# Revit family: TY-FRB-TY4131_Imperial
name_source: partatom
category: Sprinklers
revit_build: Autodesk Revit 2016 (Build: 20150220_1215(x64)
units: mm (PartAtom-declared; Revit-internal decimal feet)

## family parameters
Always vertical = Yes
Cut with Voids When Loaded = No
Maintain Annotation Orientation = No
OmniClass Number = 23.65.70.17.11.24
OmniClass Title = Fire Fighting Sprinkler Heads
Part Type = Normal
Room Calculation Point = No
Round Connector Dimension = Use Diameter
Shared = No
Work Plane-Based = No

## types (27) — shared parameters
COBie = Yes
COBie.Component.Name = Sprinklers:Upright_SIN
COBie.Type = Yes
COBie.Type.AssetType = Fixed
COBie.Type.Category = Pr_70_55_97_84:Sprinklers
COBie.Type.Manufacturer = Tyco Fire Protection Products
COBie.Type.Material = Bronze
COBie.Type.NominalHeight = 0' - 0"
COBie.Type.NominalLength = 0' - 0"
COBie.Type.NominalWidth = 0' - 0"
COBie.Type.Shape = Cylinder
COBie.Type.Size = 3/4"(DN20)
COBie.Type.WarrantyGuarantorParts = http://tycofsbp.com
Coverage = Standard
Coverage_ = Standard
K-Factor = 7.9771
Manufacturer = Tyco Fire Protection Products
Manufacturer URL = www.tyco-fire.com
Material_ = Bronze
Model = TY-FRB
Nominal Diameter 1 = 1"
Orifice = Extra Large
Orifice Size = 1"
Outside Diameter 1 = 1"
Response = Quick
Response_ = Quick
SIN No = TY4131
Takeout 1 = 2"
Technical Data Sheet No = TFP171
zero-valued in all types: COBie.Type.ReplacementCost, Style Id

## per-type parameters (varying)
| type | COBie.Component.Description | COBie.Type.Colour | COBie.Type.DurationUnit | COBie.Type.Finish | COBie.Type.ModelNumber | COBie.Type.ModelReference | COBie.Type.WarrantyDescription | Description | Finish_ | Part No | Temperature Rating |
| Upright Brass 135°F/57°C 8K ¾"(DN20) NPT_57-390-1-135 | TY-FRB Wet Upright  57.2°C K115 DN20 NPT Br | Yellow | year | Natural Brass | 57-390-1-135 | TY-FRB Wet Upright  57.2°C K115 DN20 NPT Br |  | TY-FRB Upright Brass 135°F/57°C 8K ¾" NPT | Natural Brass | 57-390-1-135 | 135 °F |
| Upright Brass 155°F/68°C 8K ¾"(DN20) NPT_57-390-1-155 | TY-FRB Wet Upright  68.3°C K115 DN20 NPT Br | Yellow | year | Natural Brass | 57-390-1-155 | TY-FRB Wet Upright  68.3°C K115 DN20 NPT Br |  | TY-FRB Upright Brass 155°F/68°C 8K ¾" NPT | Natural Brass | 57-390-1-155 | 155 °F |
| Upright Brass 175°F/79°C 8K ¾"(DN20) NPT_57-390-1-175 | TY-FRB Wet Upright  79.4°C K115 DN20 NPT Br | yellow | year | Natural Brass | 57-390-1-175 | TY-FRB Wet Upright  79.4°C K115 DN20 NPT Br |  | TY-FRB Upright Brass 175°F/79°C 8K ¾" NPT | Natural Brass | 57-390-1-175 | 175 °F |
| Upright Brass 200°F/93°C 8K ¾"(DN20) NPT_57-390-1-200 | TY-FRB Wet Upright  93.3°C K115 DN20 NPT Br | Yellow | year | Natural Brass | 57-390-1-200 | TY-FRB Wet Upright  93.3°C K115 DN20 NPT Br |  | TY-FRB Upright Brass 200°F/93°C 8K ¾" NPT | Natural Brass | 57-390-1-200 | 200 °F |
| Upright Brass 286°F/141°C 8K ¾"(DN20) NPT_57-390-1-286 | TY-FRB Wet Upright  141.1°C K115 DN20 NPT Br | Yellow | year | Natural Brass | 57-390-1-286 | TY-FRB Wet Upright  141.1°C K115 DN20 NPT Br |  | TY-FRB Upright Brass 286°F/141°C 8K ¾" NPT | Natural Brass | 57-390-1-286 | 286 °F |
| Upright Chrome 135°F/57°C 8K ¾"(DN20) NPT_57-390-3-135 | TY-FRB Wet Upright  57.2°C K115 DN20 NPT Wh9010 | White | year | Pure White | 57-390-3-135 | TY-FRB Wet Upright  57.2°C K115 DN20 NPT Wh9010 |  | TY-FRB Upright Chrome 135°F/57°C 8K ¾" NPT | White RAL9010 | 57-390-3-135 | 135 °F |
| Upright Chrome 155°F/68°C 8K ¾"(DN20) NPT_57-390-3-155 | TY-FRB Wet Upright  68.3°C K115 DN20 NPT Wh9010 | White | year | Pure White | 57-390-3-155 | TY-FRB Wet Upright  68.3°C K115 DN20 NPT Wh9010 | On-site Sprinkler Replacement Warranty | TY-FRB Upright Chrome 155°F/68°C 8K ¾" NPT | White RAL9010 | 57-390-3-155 | 155 °F |
| Upright Chrome 175°F/79°C 8K ¾"(DN20) NPT_57-390-3-175 | TY-FRB Wet Upright_175  79.4°C K115 DN20 NPT Wh9010 | White | year | Pure White | 57-390-3-175 | TY-FRB Wet Upright_175  79.4°C K115 DN20 NPT Wh9010 |  | TY-FRB Upright Chrome 175°F/79°C 8K ¾" NPT | White RAL9010 | 57-390-3-175 | 175 °F |
| Upright Chrome 200°F/93°C 8K ¾"(DN20) NPT_57-390-3-200 | TY-FRB Wet Upright  93.3°C K115 DN20 NPT Wh9010 | White | year | Pure White | 57-390-3-200 | TY-FRB Wet Upright  93.3°C K115 DN20 NPT Wh9010 |  | TY-FRB Upright Chrome 200°F/93°C 8K ¾" NPT | White RAL9010 | 57-390-3-200 | 200 °F |
| Upright Chrome 286°F/141°C 8K ¾"(DN20) NPT_57-390-3-286 | TY-FRB Wet Upright  141.1°C K115 DN20 NPT Wh9010 | White | year | Pure White | 57-390-3-286 | TY-FRB Wet Upright  141.1°C K115 DN20 NPT Wh9010 |  | TY-FRB Upright Chrome 286°F/141°C 8K ¾" NPT | White RAL9010 | 57-390-3-286 | 286 °F |
| Upright White 135°F/57°C 8K ¾"(DN20) NPT_57-390-4-135 | TY-FRB Wet Upright  57.2°C K115 DN20 NPT Wh | White | year | Signal White | 57-390-4-135 | TY-FRB Wet Upright  57.2°C K115 DN20 NPT Wh |  | TY-FRB Upright White 135°F/57°C 8K ¾" NPT | White RAL9003 | 57-390-4-135 | 135 °F |
| Upright White 155°F/68°C 8K ¾"(DN20) NPT_57-390-4-155 | TY-FRB Wet Upright  68.3°C K115 DN20 NPT Wh | White | year | Signal White | 57-390-4-155 | TY-FRB Wet Upright  68.3°C K115 DN20 NPT Wh |  | TY-FRB Upright White 155°F/68°C 8K ¾" NPT | White RAL9003 | 57-390-4-155 | 155 °F |
| Upright White 175°F/79°C 8K ¾"(DN20) NPT_57-390-4-175 | TY-FRB Wet Upright  79.4°C K115 DN20 NPT Wh | White |  | Signal White | 57-390-4-175 | TY-FRB Wet Upright  79.4°C K115 DN20 NPT Wh |  | TY-FRB Upright White 175°F/79°C 8K ¾" NPT | White RAL9003 | 57-390-4-175 | 175 °F |
| Upright White 200°F/93°C 8K ¾"(DN20) NPT_57-390-4-200 | TY-FRB Wet Upright  93.3°C K115 DN20 NPT Wh | White | year | Signal White | 57-390-4-200 | TY-FRB Wet Upright  93.3°C K115 DN20 NPT Wh |  | TY-FRB Upright White 200°F/93°C 8K ¾" NPT | White RAL9003 | 57-390-4-200 | 200 °F |
| Upright White 286°F/141°C 8K ¾"(DN20) NPT_57-390-4-286 | TY-FRB Wet Upright  141.1°C K115 DN20 NPT Wh | White | year | Signal White | 57-390-4-286 | TY-FRB Wet Upright  141.1°C K115 DN20 NPT Wh |  | TY-FRB Upright White 286°F/141°C 8K ¾" NPT | White RAL9003 | 57-390-4-286 | 286 °F |
| Upright Jet Black 155°F/68°C 8K ¾"(DN20) NPT_57-390-5-155 | TY-FRB Wet Upright  155°F K8.0 3/4 NPT Wh | Black | year | Jet Black | 57-390-5-155 | TY-FRB Wet Upright  155°F K8.0 3/4 NPT Wh |  | TY-FRB Upright Jet Black 155°F/68°C 8K ¾" NPT | Jet Black RAL9005 | 57-390-5-155 | 155 °F |
| Upright Jet Black 155°F/68°C 8K ¾"(DN20) NPT_57-390-5-200 | TY-FRB Wet Upright_Black_155   155°F K8.0 3/4 NPT Wh | Black | year | Jet Black | 57-390-5-200 | TY-FRB Wet Upright_Black_155   155°F K8.0 3/4 NPT Wh |  | TY-FRB Upright Jet Black 155°F/68°C 8K ¾" NPT | Jet Black RAL9005 | 57-390-5-200 | 155 °F |
| Upright Lead 135°F/57°C 8K ¾"(DN20) NPT_57-390-7-135 | TY-FRB Wet Upright  57.2°C K115 DN20 NPT Lead | Gray | year | Lead Coated | 57-390-7-135 | TY-FRB Wet Upright  57.2°C K115 DN20 NPT Lead |  | TY-FRB Upright Lead 135°F/57°C 8K ¾" NPT | Lead Coated | 57-390-7-135 | 135 °F |
| Upright Lead 155°F/68°C 8K ¾"(DN20) NPT_57-390-7-155 | TY-FRB Wet Upright  68.3°C K115 DN20 NPT Lead | Gray | year | Lead Coated | 57-390-7-155 | TY-FRB Wet Upright  68.3°C K115 DN20 NPT Lead |  | TY-FRB Upright Lead 155°F/68°C 8K ¾" NPT | Lead Coated | 57-390-7-155 | 155 °F |
| Upright Lead 175°F/79°C 8K ¾"(DN20) NPT_57-390-7-175 | TY-FRB Wet Upright  79.4°C K115 DN20 NPT Lead | Gray | year | Lead Coated | 57-390-7-175 | TY-FRB Wet Upright  79.4°C K115 DN20 NPT Lead |  | TY-FRB Upright Lead 175°F/79°C 8K ¾" NPT | Lead Coated | 57-390-7-175 | 175 °F |
| Upright Lead 200°F/93°C 8K ¾"(DN20) NPT_57-390-7-200 | TY-FRB Wet Upright  93.3°C K115 DN20 NPT Lead | Gray | year | Lead Coated | 57-390-7-200 | TY-FRB Wet Upright  93.3°C K115 DN20 NPT Lead |  | TY-FRB Upright Lead 200°F/93°C 8K ¾" NPT | Lead Coated | 57-390-7-200 | 200 °F |
| Upright Lead 286°F/141°C 8K ¾"(DN20) NPT_57-390-7-286 | TY-FRB Wet Upright  141.1°C K115 DN20 NPT Lead | Gray | year | Lead Coated | 57-390-7-286 | TY-FRB Wet Upright  141.1°C K115 DN20 NPT Lead |  | TY-FRB Upright Lead 286°F/141°C 8K ¾" NPT | Lead Coated | 57-390-7-286 | 286 °F |
| Upright Chrome 135°F/57°C 8K ¾"(DN20) NPT_57-390-9-135 | TY-FRB Wet Upright  57.2°C K115 DN20 NPT Chr | Silver | year | Chrome Plated | 57-390-9-135 | TY-FRB Wet Upright  57.2°C K115 DN20 NPT Chr |  | TY-FRB Upright Chrome 135°F/57°C 8K ¾" NPT | Chrome Plated | 57-390-9-135 | 135 °F |
| Upright Chrome 155°F/68°C 8K ¾"(DN20) NPT_57-390-9-155 | TY-FRB Wet Upright  68.3°C K115 DN20 NPT Chr | Silver | year | Chrome Plated | 57-390-9-155 | TY-FRB Wet Upright  68.3°C K115 DN20 NPT Chr |  | TY-FRB Upright Chrome 155°F/68°C 8K ¾" NPT | Chrome Plated | 57-390-9-155 | 155 °F |
| Upright Chrome 175°F/79°C 8K ¾"(DN20) NPT_57-390-9-175 | TY-FRB Wet Upright  79.4°C K115 DN20 NPT Chr | Silver | year | Chrome Plated | 57-390-9-175 | TY-FRB Wet Upright  79.4°C K115 DN20 NPT Chr |  | TY-FRB Upright Chrome 175°F/79°C 8K ¾" NPT | Chrome Plated | 57-390-9-175 | 175 °F |
| Upright Chrome 200°F/93°C 8K ¾"(DN20) NPT_57-390-9-200 | TY-FRB Wet Upright  93.3°C K115 DN20 NPT Chr | Silver | year | Chrome Plated | 57-390-9-200 | TY-FRB Wet Upright  93.3°C K115 DN20 NPT Chr |  | TY-FRB Upright Chrome 200°F/93°C 8K ¾" NPT | Chrome Plated | 57-390-9-200 | 200 °F |
| Upright Chrome 286°F/141°C 8K ¾"(DN20) NPT_57-390-9-286 | TY-FRB Wet Upright  141.1°C K115 DN20 NPT Chr | Silver | year | Chrome Plated | 57-390-9-286 | TY-FRB Wet Upright  141.1°C K115 DN20 NPT Chr |  | TY-FRB Upright Chrome 286°F/141°C 8K ¾" NPT | Chrome Plated | 57-390-9-286 | 286 °F |

## geometry (parser evidence)
native form markers: Blend x2, Sweep x63
no freeform markers — native parametric forms only
